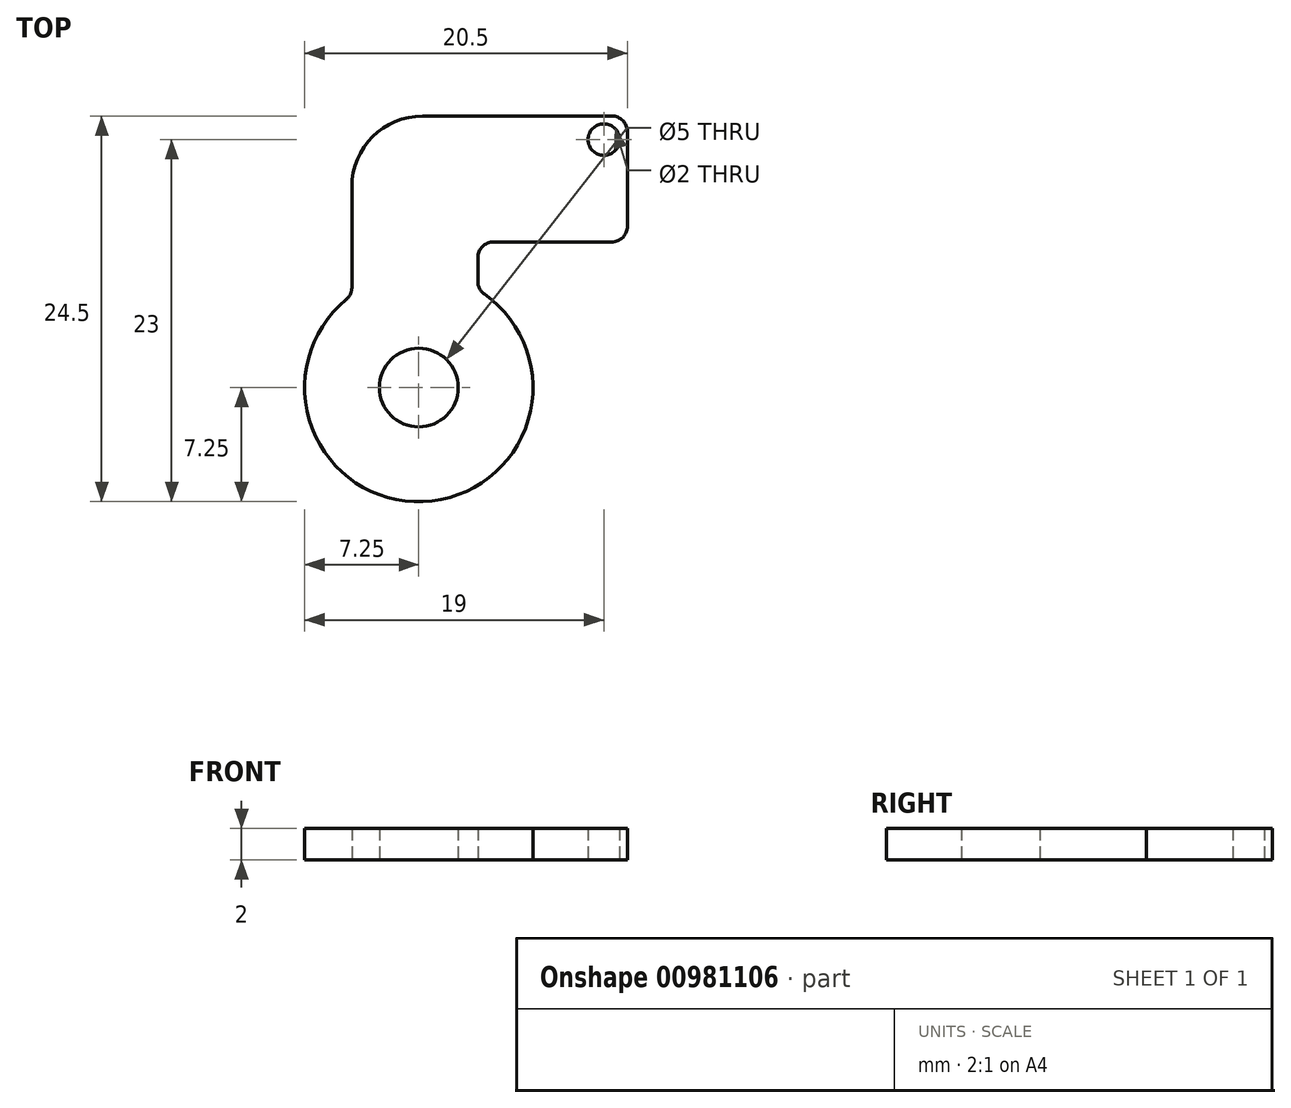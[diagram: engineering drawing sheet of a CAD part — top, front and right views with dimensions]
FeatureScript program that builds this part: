
annotation { "Feature Type Name" : "Feature", "Feature Type Description" : "" }
export const myFeature = defineFeature(function(context is Context, id is Id, definition is map)
    precondition{}
    {
        {
            var Q0;
            Q0=qCreatedBy(makeId("Top.planeOp"),FACE);
            var sketch = newSketch(context, id + "F0", { "sketchPlane" : qUnion([Q0])});
            skArc(sketch, "E0", {"start": v(-4.61, 5.6) * mm, "mid": v(0.28, -7.24) * mm, "end": v(4.17, 5.93) * mm});
            skCircle(sketch, "E1", {"center": v(0, 0) * mm, "radius": 2.5 * mm});
            skLineSegment(sketch, "E2.top", {"start": v(0.25, 17.25) * mm, "end": v(12.25, 17.25) * mm});
            skLineSegment(sketch, "E2.left", {"start": v(-4.25, 6.36) * mm, "end": v(-4.25, 12.75) * mm});
            skLineSegment(sketch, "E2.right", {"start": v(3.75, 6.75) * mm, "end": v(3.75, 8.25) * mm});
            skLineSegment(sketch, "E3", {"start": v(13.25, 16.25) * mm, "end": v(13.25, 10.25) * mm});
            skLineSegment(sketch, "E4", {"start": v(4.75, 9.25) * mm, "end": v(12.25, 9.25) * mm});
            skPoint(sketch, "E5.visualSharp", {"position": v(-4.25, 17.25) * mm});
            skArc(sketch, "E5.filletArc", {"start": v(0.25, 17.25) * mm, "mid": v(-2.93, 15.93) * mm, "end": v(-4.25, 12.75) * mm});
            skPoint(sketch, "E6.visualSharp", {"position": v(3.75, 9.25) * mm});
            skArc(sketch, "E6.filletArc", {"start": v(4.75, 9.25) * mm, "mid": v(4.04, 8.96) * mm, "end": v(3.75, 8.25) * mm});
            skPoint(sketch, "E7.visualSharp", {"position": v(13.25, 9.25) * mm});
            skArc(sketch, "E7.filletArc", {"start": v(12.25, 9.25) * mm, "mid": v(12.96, 9.54) * mm, "end": v(13.25, 10.25) * mm});
            skPoint(sketch, "E8.visualSharp", {"position": v(13.25, 17.25) * mm});
            skArc(sketch, "E8.filletArc", {"start": v(13.25, 16.25) * mm, "mid": v(12.96, 16.96) * mm, "end": v(12.25, 17.25) * mm});
            skPoint(sketch, "E9.visualSharp", {"position": v(3.75, 6.2) * mm});
            skArc(sketch, "E9.filletArc", {"start": v(3.75, 6.75) * mm, "mid": v(3.86, 6.28) * mm, "end": v(4.17, 5.93) * mm});
            skPoint(sketch, "E10.visualSharp", {"position": v(-4.25, 5.87) * mm});
            skArc(sketch, "E10.filletArc", {"start": v(-4.61, 5.6) * mm, "mid": v(-4.35, 5.94) * mm, "end": v(-4.25, 6.36) * mm});
            skCircle(sketch, "E11", {"center": v(11.75, 15.75) * mm, "radius": 1 * mm});
            skSolve(sketch);
        }
        {
            var Q0;
            Q0 = qSketchRegion(id + "F0", true);
            extrude(context, id + "F1", {"entities" : qUnion([Q0]), "depth" : 2 * mm, "offsetDistance" : 25 * mm});
        }
    });
